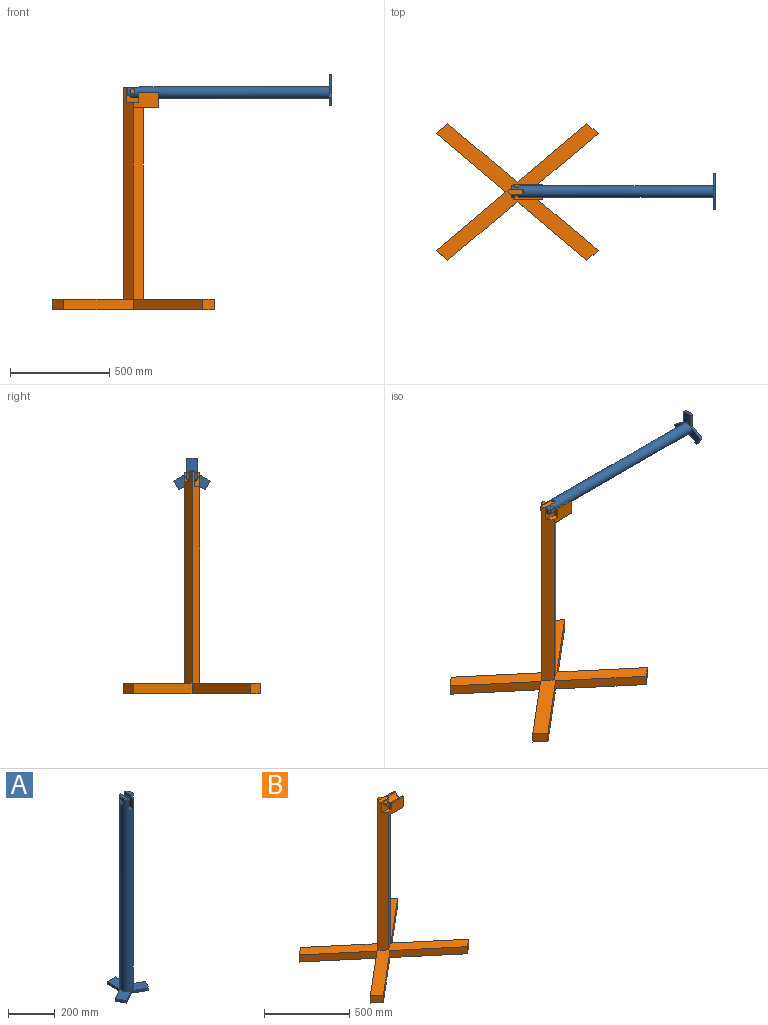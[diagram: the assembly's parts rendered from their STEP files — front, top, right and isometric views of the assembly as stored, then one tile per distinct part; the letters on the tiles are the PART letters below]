
ASSEMBLY  parts=2 mates=1
PART A: 23 faces, bbox 182.8x158.3x1028.7 mm
  f0: plane 38.94x16.63mm, normal (0,0,1), area 511.6mm2, adj f2,f17,f20
  f1: plane 38.94x16.63mm, normal (0,0,1), area 511.6mm2, adj f2,f18,f19
  f2: cylinder r=29.33mm len=1016mm, axis (0,0,-1), area 182345.7mm2, adj f0,f1,f3,f4,f15,f16,f17,f18
  f3: plane 76.2x50.8mm, normal (0,0,1), area 3342.6mm2, adj f2,f5,f12,f13
  f4: plane 91.39x82.09mm, normal (0,0,1), area 3342.6mm2, adj f2,f6,f7,f8
  f5: plane 76.2x12.7mm, normal (-1,0,0), area 967.7mm2, adj f3,f6,f13,f14
  f6: plane 65.99x38.1mm, normal (-0.5,0.87,0), area 967.7mm2, adj f4,f5,f7,f14
  f7: plane 43.99x25.4mm, normal (-0.87,-0.5,0), area 645.2mm2, adj f4,f6,f8,f14
  f8: plane 65.99x38.1mm, normal (0.5,-0.87,0), area 967.7mm2, adj f4,f7,f9,f14
  f9: plane 65.99x38.1mm, normal (-0.5,-0.87,0), area 967.7mm2, adj f8,f10,f14,f15
  f10: plane 43.99x25.4mm, normal (0.87,-0.5,0), area 645.2mm2, adj f9,f11,f14,f15
  f11: plane 65.99x38.1mm, normal (0.5,0.87,0), area 967.7mm2, adj f10,f12,f14,f15
  f12: plane 76.2x12.7mm, normal (1,0,0), area 967.7mm2, adj f3,f11,f13,f14
  f13: plane 50.8x12.7mm, normal (0,1,0), area 645.2mm2, adj f3,f5,f12,f14
  f14: plane 182.78x158.29mm, normal (0,0,-1), area 12730.3mm2, adj f5,f6,f7,f8,f9,f10,f11,f12
  f15: plane 91.39x82.09mm, normal (0,0,1), area 3342.6mm2, adj f2,f9,f10,f11
  f16: plane 58.66x25.4mm, normal (0,0,1), area 1442mm2, adj f2,f17,f18
  f17: plane 63.5x52.87mm, normal (1,0,0), area 2702.9mm2, adj f0,f2,f16,f20,f22
  f18: plane 63.5x52.87mm, normal (-1,0,0), area 2702.9mm2, adj f1,f2,f16,f19,f21
  f19: plane 21.24x13.93mm, normal (0,-0.84,0.55), area 216.2mm2, adj f1,f2,f18
  f20: plane 21.24x13.93mm, normal (0,-0.84,0.55), area 216.2mm2, adj f0,f2,f17
  f21: cylinder r=12.7mm len=25.4mm, axis (1,0,0), area 1133.6mm2, adj f2,f18
  f22: cylinder r=12.7mm len=25.4mm, axis (1,0,0), area 1133.8mm2, adj f2,f17
PART B: 37 faces, bbox 815.6x687.6x1117.6 mm
  f0: plane 1066.8x50.8mm, normal (-0.6,0.8,0), area 65499.2mm2, adj f5,f9,f10,f11,f12,f26,f32
  f1: cylinder r=29.21mm len=101.6mm, axis (1,0,0), area 9323.4mm2, adj f2,f3,f4,f7,f29,f31
  f2: plane 101.6x8.89mm, normal (0,0,1), area 903.2mm2, adj f1,f7,f27,f29
  f3: plane 101.6x8.89mm, normal (0,0,1), area 903.2mm2, adj f1,f7,f26,f31
  f4: plane 55.88x25.4mm, normal (1,0,0), area 1395.3mm2, adj f1,f5,f6,f11
  f5: plane 59.27x52.97mm, normal (0,1,0), area 2632.9mm2, adj f0,f4,f11,f32,f35
  f6: plane 77.47x59.27mm, normal (0,-1,0), area 4084.7mm2, adj f4,f10,f11,f29,f30,f34
  f7: plane 76.2x76.2mm, normal (1,0,0), area 4466.2mm2, adj f1,f2,f3,f26,f27,f28
  f8: plane 963.93x50.8mm, normal (0.6,-0.8,0), area 61209.6mm2, adj f9,f10,f12,f28
  f9: plane 963.93x50.8mm, normal (0.6,0.8,0), area 61209.6mm2, adj f0,f8,f12,f28
  f10: plane 1066.8x50.8mm, normal (-0.6,-0.8,0), area 64462.2mm2, adj f0,f6,f8,f11,f12,f27,f30
  f11: plane 76.2x25.4mm, normal (0,0,1), area 1720.4mm2, adj f0,f4,f5,f6,f10
  f12: plane 815.65x687.59mm, normal (0,0,1), area 139198.5mm2, adj f0,f8,f9,f10,f13,f14,f15,f16
  f13: plane 349.56x294.68mm, normal (-0.64,-0.76,0), area 23225.8mm2, adj f12,f14,f24,f25
  f14: plane 349.56x294.68mm, normal (-0.64,0.76,0), area 23225.8mm2, adj f12,f13,f15,f25
  f15: plane 58.26x50.8mm, normal (-0.64,-0.76,0), area 3871mm2, adj f12,f14,f16,f25
  f16: plane 349.56x294.68mm, normal (0.64,-0.76,0), area 23225.8mm2, adj f12,f15,f17,f25
  f17: plane 349.56x294.68mm, normal (-0.64,-0.76,0), area 23225.8mm2, adj f12,f16,f18,f25
  f18: plane 58.26x50.8mm, normal (0.64,-0.76,0), area 3871mm2, adj f12,f17,f19,f25
  f19: plane 349.56x294.68mm, normal (0.64,0.76,0), area 23225.8mm2, adj f12,f18,f20,f25
  f20: plane 349.56x294.68mm, normal (0.64,-0.76,0), area 23225.8mm2, adj f12,f19,f21,f25
  f21: plane 58.26x50.8mm, normal (0.64,0.76,0), area 3871mm2, adj f12,f20,f22,f25
  f22: plane 349.56x294.68mm, normal (-0.64,0.76,0), area 23225.8mm2, adj f12,f21,f23,f25
  f23: plane 349.56x294.68mm, normal (0.64,0.76,0), area 23225.8mm2, adj f12,f22,f24,f25
  f24: plane 58.26x50.8mm, normal (-0.64,0.76,0), area 3871mm2, adj f12,f13,f23,f25
  f25: plane 815.65x687.59mm, normal (0,0,-1), area 143069.5mm2, adj f13,f14,f15,f16,f17,f18,f19,f20
  f26: plane 127x76.2mm, normal (0,1,0), area 9009.3mm2, adj f0,f3,f7,f28,f31,f32
  f27: plane 127x76.2mm, normal (0,-1,0), area 8387.1mm2, adj f2,f7,f10,f28,f29,f30
  f28: plane 127x76.2mm, normal (0,0,-1), area 7741.9mm2, adj f7,f8,f9,f26,f27
  f29: plane 50.8x25.4mm, normal (-1,0,0), area 979.1mm2, adj f1,f2,f6,f27,f30
  f30: plane 59.27x25.4mm, normal (0,0,1), area 1075.3mm2, adj f6,f10,f27,f29
  f31: plane 26.3x25.4mm, normal (-1,0,0), area 356.9mm2, adj f1,f3,f26,f32
  f32: plane 59.27x25.4mm, normal (0,0,1), area 1075.3mm2, adj f0,f5,f26,f31
  f33: plane 25.4x25.4mm, normal (0,-1,0), area 506.7mm2, adj f34
  f34: cylinder r=12.7mm len=25.4mm, axis (0,1,0), area 2026.8mm2, adj f6,f33
  f35: cylinder r=12.7mm len=25.4mm, axis (0,1,0), area 2026.8mm2, adj f5,f36
  f36: plane 25.4x25.4mm, normal (0,1,0), area 506.7mm2, adj f35
PLACE A rot(axis=(0.58,-0.58,-0.58),120deg) t=(990.17,-1.01,157.02)mm
PLACE B t=(70.99,-56.24,-869.1)mm fixed
MATE revolute B.f34 <-> A.f21  axis (0,1,0) through (-0.43,11.69,178.65)mm
